# Revit family: Vancouver 90 Square LED
name_source: partatom
category: Lighting Fixtures
revit_build: Autodesk Revit 2018 (Build: 20170927_1515(x64)
units: mm (PartAtom-declared; Revit-internal decimal feet)

## family parameters
Always vertical = Yes
Cut with Voids When Loaded = No
Host = Ceiling
Light Source = Yes
OmniClass Number = 23.80.70.11
OmniClass Title = Luminaries for Internal Lighting
Part Type = Normal
Room Calculation Point = No
Round Connector Dimension = Use Diameter
Shared = No

## types (2) — shared parameters
Color Filter = 16777215
Dimming Lamp Color Temperature Shift = <None>
Emit from Line Length = 610 mm

## per-type parameters (varying)
| type | ADA compliant | Dimmable | Dimming Method | Driver Included | Driver Required | Efficacy (lm/w) | Electrical Class | Lamp | Length of supplied cable | Light Source Fixed | Location Rating | Main Finish | Main Material | Photometric Web File | Product Code | Product Location | Product Name | Product SKU | Tilt Angle |
| CE |  |  |  |  |  |  |  |  |  |  |  |  |  | generic |  |  |  |  | 60.00° |
| ETL | Yes | Yes | Driver Dependent | No | Yes | 123.77 | 2 | LED | 450mm | Yes | Wet | Clear Acrylic | Acrylic | 5753_CXA1512-3000K_170525 IES.ies | 5753 | Bathroom | Vancouver 90 Round LED | 1229013 | 0.00° |

## geometry (parser evidence)
native form markers: Sweep x1
no freeform markers — native parametric forms only
